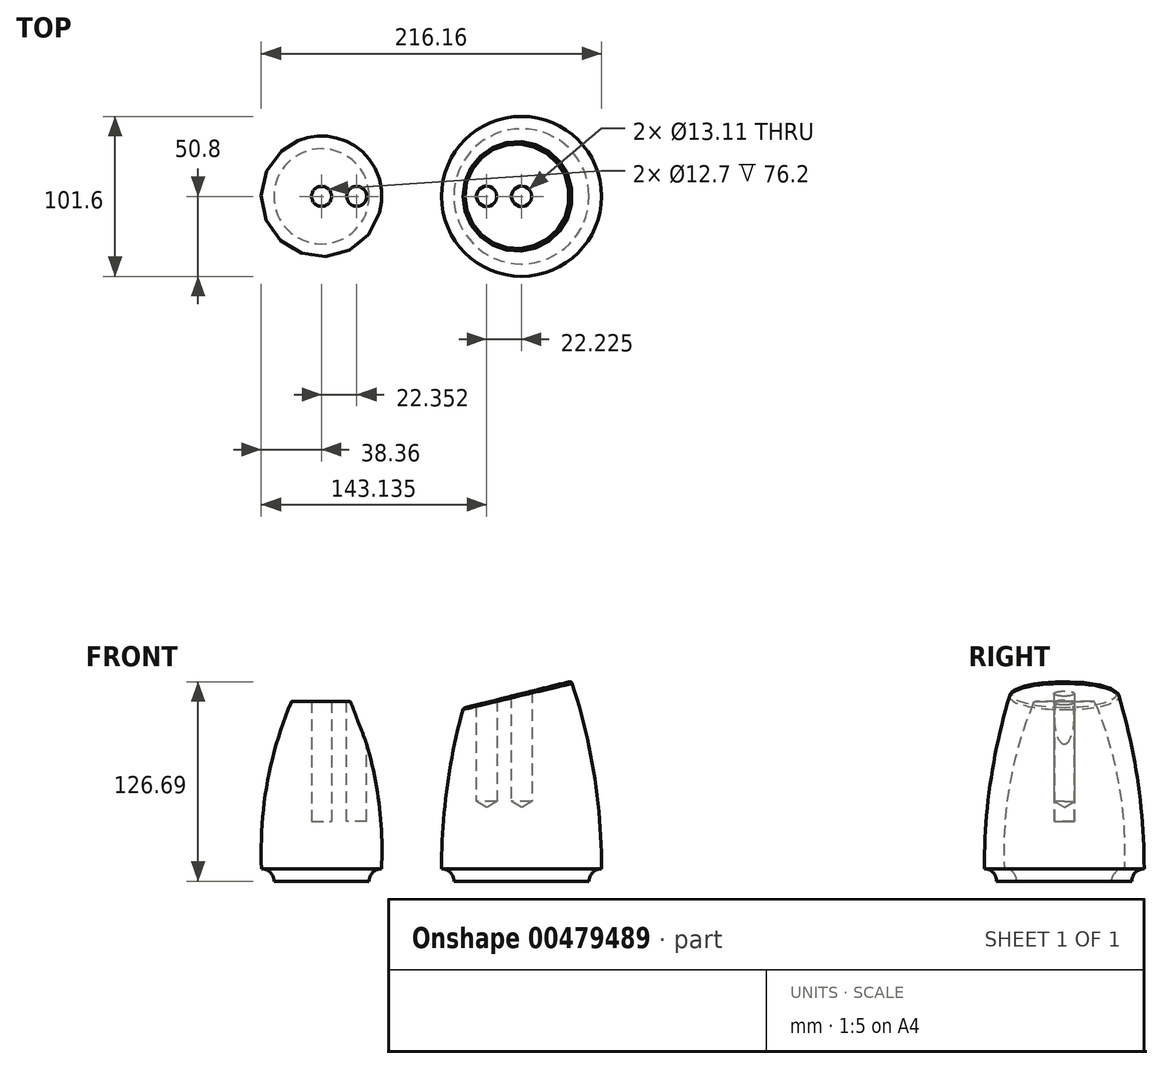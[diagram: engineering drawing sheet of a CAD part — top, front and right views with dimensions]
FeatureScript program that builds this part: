
annotation { "Feature Type Name" : "Feature", "Feature Type Description" : "" }
export const myFeature = defineFeature(function(context is Context, id is Id, definition is map)
    precondition{}
    {
        {
            var Q0;
            Q0=qCreatedBy(makeId("Front.planeOp"),FACE);
            var sketch = newSketch(context, id + "F0", { "sketchPlane" : qUnion([Q0])});
            skLineSegment(sketch, "E0", {"start": v(0, 0) * mm, "end": v(0, 152.4) * mm});
            skLineSegment(sketch, "E1", {"start": v(0, 0) * mm, "end": v(30.23, 0) * mm});
            skLineSegment(sketch, "E2", {"start": v(0, 114.3) * mm, "end": v(19.05, 114.3) * mm});
            skArc(sketch, "E3", {"start": v(38.1, 7.87) * mm, "mid": v(34.53, 62.15) * mm, "end": v(19.05, 114.3) * mm});
            skArc(sketch, "E4", {"start": v(38.1, 7.87) * mm, "mid": v(32.53, 5.57) * mm, "end": v(30.23, 0) * mm});
            skLineSegment(sketch, "E5.bottom", {"start": v(16, 114.3) * mm, "end": v(28.7, 114.3) * mm});
            skLineSegment(sketch, "E5.top", {"start": v(16, 38.1) * mm, "end": v(28.7, 38.1) * mm});
            skLineSegment(sketch, "E5.left", {"start": v(16, 114.3) * mm, "end": v(16, 38.1) * mm});
            skLineSegment(sketch, "E5.right", {"start": v(28.7, 114.3) * mm, "end": v(28.7, 38.1) * mm});
            skLineSegment(sketch, "E6", {"start": v(22.35, 38.1) * mm, "end": v(22.35, 114.3) * mm});
            skLineSegment(sketch, "E7", {"start": v(6.35, 114.3) * mm, "end": v(6.35, 38.1) * mm});
            skLineSegment(sketch, "E8", {"start": v(6.35, 38.1) * mm, "end": v(0, 38.1) * mm});
            skSolve(sketch);
        }
        {
            var Q0;
            {var subQ5=sQuery(id+"F0.wireOp",EDGE,"E1");Q0=makeQuery(id+"F0.imprint","IMPRINT",FACE,{"disambiguationData":[TD([[makeQuery(id+"F0.imprint","IMPRINT",EDGE,{"derivedFrom":subQ5}),1.0]])]});}
            var Q1;
            {var subQ5=sQuery(id+"F0.wireOp",EDGE,"E5.top");Q1=makeQuery(id+"F0.imprint","IMPRINT",FACE,{"disambiguationData":[TD([[makeQuery(id+"F0.imprint","IMPRINT",EDGE,{"derivedFrom":subQ5}),1.0]])]});}
            var Q2;
            {var subQ0=sQuery(id+"F0.wireOp",EDGE,"E5.left");Q2=makeQuery(id+"F0.imprint","IMPRINT",FACE,{"disambiguationData":[TD([[makeQuery(id+"F0.imprint","IMPRINT",EDGE,{"derivedFrom":subQ0}),1.0]])]});}
            var Q3;
            Q3=sQuery(id+"F0.wireOp",EDGE,"E0");
            revolve(context, id + "F1", {"entities" : qUnion([Q0, Q1, Q2]), "axis" : qUnion([Q3]), "revolveType" : RevolveType.FULL});
        }
        {
            var Q0;
            {var subQ4=sQuery(id+"F0.wireOp",EDGE,"E7");Q0=makeQuery(id+"F0.imprint","IMPRINT",FACE,{"disambiguationData":[TD([[makeQuery(id+"F0.imprint","IMPRINT",EDGE,{"derivedFrom":subQ4}),-1.0]])]});}
            var Q1;
            Q1=sQuery(id+"F0.wireOp",EDGE,"E0");
            revolve(context, id + "F2", {"operationType" : NewBodyOperationType.REMOVE, "entities" : qUnion([Q0]), "axis" : qUnion([Q1]), "revolveType" : RevolveType.FULL, "oppositeDirection" : true});
        }
        {
            var Q0;
            {var subQ0=sQuery(id+"F0.wireOp",EDGE,"E5.right");var subQ1=sQuery(id+"F0.wireOp",EDGE,"E3");var subQ2=makeQuery(id+"F0.imprint","INTERSECT",VERTEX,{"derivedFrom":[subQ1,subQ0]});Q0=makeQuery(id+"F0.imprint","IMPRINT",FACE,{"disambiguationData":[TD([[makeQuery(id+"F0.imprint","IMPRINT",EDGE,{"disambiguationData":[TD([[subQ2,-1.0]])],"derivedFrom":subQ1}),-1.0]])]});}
            var Q1;
            {var subQ0=sQuery(id+"F0.wireOp",EDGE,"E5.right");var subQ1=sQuery(id+"F0.wireOp",EDGE,"E3");var subQ2=makeQuery(id+"F0.imprint","INTERSECT",VERTEX,{"derivedFrom":[subQ1,subQ0]});Q1=makeQuery(id+"F0.imprint","IMPRINT",FACE,{"disambiguationData":[TD([[makeQuery(id+"F0.imprint","IMPRINT",EDGE,{"disambiguationData":[TD([[subQ2,-1.0]])],"derivedFrom":subQ1}),1.0]])]});}
            var Q2;
            Q2=sQuery(id+"F0.wireOp",EDGE,"E6");
            revolve(context, id + "F3", {"operationType" : NewBodyOperationType.REMOVE, "entities" : qUnion([Q0, Q1]), "axis" : qUnion([Q2]), "revolveType" : RevolveType.FULL, "oppositeDirection" : true});
        }
        {
            var Q0;
            {var subQ0=sQuery(id+"F0.wireOp",EDGE,"E5.bottom");var subQ2=sQuery(id+"F0.wireOp",EDGE,"E5.right");var subQ3=sQuery(id+"F0.wireOp",EDGE,"E3");var subQ5=makeQuery(id+"F3.boolean.opBoolean","COPY",FACE,{"derivedFrom":makeQuery(id+"F3.opRevolve","SWEPT_FACE",FACE,{"disambiguationData":[OSD([subQ2])]})});Q0=makeQuery(id+"F1Nw9IQKKF3mM8D_1.5.F3.boolean.opBoolean","SPLIT",EDGE,{"disambiguationData":[TD([subQ5])],"derivedFrom":makeQuery(id+"F1Nw9IQKKF3mM8D_1.4.F3.boolean.opBoolean","SPLIT",EDGE,{"disambiguationData":[TD([subQ5])],"derivedFrom":makeQuery(id+"F1Nw9IQKKF3mM8D_1.3.F3.boolean.opBoolean","SPLIT",EDGE,{"disambiguationData":[TD([subQ5])],"derivedFrom":makeQuery(id+"F1Nw9IQKKF3mM8D_1.2.F3.boolean.opBoolean","SPLIT",EDGE,{"disambiguationData":[TD([subQ5])],"derivedFrom":makeQuery(id+"F1Nw9IQKKF3mM8D_1.1.F3.boolean.opBoolean","SPLIT",EDGE,{"disambiguationData":[OD(0.0)],"derivedFrom":makeQuery(id+"F1.opRevolve","SWEPT_EDGE",EDGE,{"disambiguationData":[OSD([subQ3,subQ0])]})})})})})});}
            var Q1;
            {var subQ0=sQuery(id+"F0.wireOp",EDGE,"E5.bottom");var subQ2=sQuery(id+"F0.wireOp",EDGE,"E5.right");var subQ3=sQuery(id+"F0.wireOp",EDGE,"E3");var subQ5=makeQuery(id+"F1Nw9IQKKF3mM8D_1.4.F3.opRevolve","SWEPT_FACE",FACE,{"disambiguationData":[OSD([subQ2])]});var subQ6=makeQuery(id+"F3.boolean.opBoolean","COPY",FACE,{"derivedFrom":makeQuery(id+"F3.opRevolve","SWEPT_FACE",FACE,{"disambiguationData":[OSD([subQ2])]})});Q1=makeQuery(id+"F1Nw9IQKKF3mM8D_1.5.F3.boolean.opBoolean","SPLIT",EDGE,{"disambiguationData":[TD([makeQuery(id+"F1Nw9IQKKF3mM8D_1.4.F3.boolean.opBoolean","COPY",FACE,{"derivedFrom":subQ5})])],"derivedFrom":makeQuery(id+"F1Nw9IQKKF3mM8D_1.4.F3.boolean.opBoolean","SPLIT",EDGE,{"disambiguationData":[TD([subQ6])],"derivedFrom":makeQuery(id+"F1Nw9IQKKF3mM8D_1.3.F3.boolean.opBoolean","SPLIT",EDGE,{"disambiguationData":[TD([subQ6])],"derivedFrom":makeQuery(id+"F1Nw9IQKKF3mM8D_1.2.F3.boolean.opBoolean","SPLIT",EDGE,{"disambiguationData":[TD([subQ6])],"derivedFrom":makeQuery(id+"F1Nw9IQKKF3mM8D_1.1.F3.boolean.opBoolean","SPLIT",EDGE,{"disambiguationData":[OD(0.0)],"derivedFrom":makeQuery(id+"F1.opRevolve","SWEPT_EDGE",EDGE,{"disambiguationData":[OSD([subQ3,subQ0])]})})})})})});}
            var Q2;
            {var subQ0=sQuery(id+"F0.wireOp",EDGE,"E5.bottom");var subQ2=sQuery(id+"F0.wireOp",EDGE,"E5.right");var subQ3=makeQuery(id+"F1Nw9IQKKF3mM8D_1.3.F3.opRevolve","SWEPT_FACE",FACE,{"disambiguationData":[OSD([subQ2])]});var subQ4=sQuery(id+"F0.wireOp",EDGE,"E3");var subQ6=makeQuery(id+"F3.boolean.opBoolean","COPY",FACE,{"derivedFrom":makeQuery(id+"F3.opRevolve","SWEPT_FACE",FACE,{"disambiguationData":[OSD([subQ2])]})});Q2=makeQuery(id+"F1Nw9IQKKF3mM8D_1.4.F3.boolean.opBoolean","SPLIT",EDGE,{"disambiguationData":[TD([makeQuery(id+"F1Nw9IQKKF3mM8D_1.3.F3.boolean.opBoolean","COPY",FACE,{"derivedFrom":subQ3})])],"derivedFrom":makeQuery(id+"F1Nw9IQKKF3mM8D_1.3.F3.boolean.opBoolean","SPLIT",EDGE,{"disambiguationData":[TD([subQ6])],"derivedFrom":makeQuery(id+"F1Nw9IQKKF3mM8D_1.2.F3.boolean.opBoolean","SPLIT",EDGE,{"disambiguationData":[TD([subQ6])],"derivedFrom":makeQuery(id+"F1Nw9IQKKF3mM8D_1.1.F3.boolean.opBoolean","SPLIT",EDGE,{"disambiguationData":[OD(0.0)],"derivedFrom":makeQuery(id+"F1.opRevolve","SWEPT_EDGE",EDGE,{"disambiguationData":[OSD([subQ4,subQ0])]})})})})});}
            var Q3;
            {var subQ0=sQuery(id+"F0.wireOp",EDGE,"E5.bottom");var subQ2=sQuery(id+"F0.wireOp",EDGE,"E3");var subQ4=sQuery(id+"F0.wireOp",EDGE,"E5.right");var subQ5=makeQuery(id+"F1Nw9IQKKF3mM8D_1.2.F3.opRevolve","SWEPT_FACE",FACE,{"disambiguationData":[OSD([subQ4])]});Q3=makeQuery(id+"F1Nw9IQKKF3mM8D_1.3.F3.boolean.opBoolean","SPLIT",EDGE,{"disambiguationData":[TD([makeQuery(id+"F1Nw9IQKKF3mM8D_1.2.F3.boolean.opBoolean","COPY",FACE,{"derivedFrom":subQ5})])],"derivedFrom":makeQuery(id+"F1Nw9IQKKF3mM8D_1.2.F3.boolean.opBoolean","SPLIT",EDGE,{"disambiguationData":[TD([makeQuery(id+"F3.boolean.opBoolean","COPY",FACE,{"derivedFrom":makeQuery(id+"F3.opRevolve","SWEPT_FACE",FACE,{"disambiguationData":[OSD([subQ4])]})})])],"derivedFrom":makeQuery(id+"F1Nw9IQKKF3mM8D_1.1.F3.boolean.opBoolean","SPLIT",EDGE,{"disambiguationData":[OD(0.0)],"derivedFrom":makeQuery(id+"F1.opRevolve","SWEPT_EDGE",EDGE,{"disambiguationData":[OSD([subQ2,subQ0])]})})})});}
            var Q4;
            {var subQ0=sQuery(id+"F0.wireOp",EDGE,"E5.bottom");var subQ1=sQuery(id+"F0.wireOp",EDGE,"E3");var subQ2=sQuery(id+"F0.wireOp",EDGE,"E5.right");Q4=makeQuery(id+"F1Nw9IQKKF3mM8D_1.2.F3.boolean.opBoolean","SPLIT",EDGE,{"disambiguationData":[TD([makeQuery(id+"F1Nw9IQKKF3mM8D_1.1.F3.boolean.opBoolean","COPY",FACE,{"derivedFrom":makeQuery(id+"F1Nw9IQKKF3mM8D_1.1.F3.opRevolve","SWEPT_FACE",FACE,{"disambiguationData":[OSD([subQ2])]})})])],"derivedFrom":makeQuery(id+"F1Nw9IQKKF3mM8D_1.1.F3.boolean.opBoolean","SPLIT",EDGE,{"disambiguationData":[OD(0.0)],"derivedFrom":makeQuery(id+"F1.opRevolve","SWEPT_EDGE",EDGE,{"disambiguationData":[OSD([subQ1,subQ0])]})})});}
            var Q5;
            Q5=makeQuery(id+"F1Nw9IQKKF3mM8D_1.1.F3.boolean.opBoolean","SPLIT",EDGE,{"disambiguationData":[OD(1.0)],"derivedFrom":makeQuery(id+"F1.opRevolve","SWEPT_EDGE",EDGE,{"disambiguationData":[OSD([sQuery(id+"F0.wireOp",EDGE,"E3"),sQuery(id+"F0.wireOp",EDGE,"E5.bottom")])]})});
            fillet(context, id + "F4", {"entities" : qUnion([Q0, Q1, Q2, Q3, Q4, Q5]), "radius" : 1.6 * mm, "tangentPropagation" : true, "allowEdgeOverflow" : false});
        }
        {
            var Q0;
            Q0=qCreatedBy(makeId("Front.planeOp"),FACE);
            var sketch = newSketch(context, id + "F5", { "sketchPlane" : qUnion([Q0])});
            skLineSegment(sketch, "E9.bottom", {"start": v(127, 0) * mm, "end": v(76.2, 0) * mm});
            skLineSegment(sketch, "E9.top", {"start": v(127, 127) * mm, "end": v(76.2, 127) * mm});
            skLineSegment(sketch, "E9.left", {"start": v(127, 0) * mm, "end": v(127, 127) * mm});
            skLineSegment(sketch, "E9.right", {"start": v(76.2, 0) * mm, "end": v(76.2, 127) * mm});
            skArc(sketch, "E10", {"start": v(95.25, 127) * mm, "mid": v(81, 68.2) * mm, "end": v(76.2, 7.87) * mm});
            skArc(sketch, "E11", {"start": v(84.07, 0) * mm, "mid": v(81.77, 5.57) * mm, "end": v(76.2, 7.87) * mm});
            skLineSegment(sketch, "E12", {"start": v(158.75, 127) * mm, "end": v(76.2, 106.42) * mm});
            skLineSegment(sketch, "E13", {"start": v(127, 127) * mm, "end": v(158.75, 127) * mm});
            skSolve(sketch);
        }
        {
            var Q0;
            {var subQ0=sQuery(id+"F5.wireOp",EDGE,"E11");Q0=makeQuery(id+"F5.imprint","IMPRINT",FACE,{"disambiguationData":[TD([[makeQuery(id+"F5.imprint","IMPRINT",EDGE,{"derivedFrom":subQ0}),-1.0]])]});}
            var Q1;
            {var subQ1=sQuery(id+"F5.wireOp",EDGE,"E9.top");var subQ3=sQuery(id+"F5.wireOp",EDGE,"E10");var subQ4=makeQuery(id+"F5.imprint","INTERSECT",VERTEX,{"derivedFrom":[subQ1,subQ3]});Q1=makeQuery(id+"F5.imprint","IMPRINT",FACE,{"disambiguationData":[TD([[makeQuery(id+"F5.imprint","IMPRINT",EDGE,{"disambiguationData":[TD([[subQ4,-1.0]])],"derivedFrom":subQ3}),1.0]])]});}
            var Q2;
            Q2=sQuery(id+"F5.wireOp",EDGE,"E9.left");
            revolve(context, id + "F6", {"entities" : qUnion([Q0, Q1]), "axis" : qUnion([Q2]), "revolveType" : RevolveType.FULL});
        }
        {
            var Q0;
            Q0=makeQuery(id+"F6.opRevolve","SWEPT_FACE",FACE,{"disambiguationData":[OSD([sQuery(id+"F5.wireOp",EDGE,"E9.top")])]});
            var sketch = newSketch(context, id + "F7", { "sketchPlane" : qUnion([Q0])});
            skPoint(sketch, "E14", {"position": v(127, 0) * mm});
            skPoint(sketch, "E15", {"position": v(104.77, 0) * mm});
            skSolve(sketch);
        }
        {
            var Q0;
            Q0=sQuery(id+"F7.wireOp",VERTEX,"E14");
            var Q1;
            Q1=sQuery(id+"F7.wireOp",VERTEX,"E15");
            var Q2;
            Q2=makeQuery(id+"F6.opRevolve","SWEPT_BODY",BODY,{"disambiguationData":[OSD([sQuery(id+"F5.wireOp",EDGE,"E9.bottom"),sQuery(id+"F5.wireOp",EDGE,"E9.top"),sQuery(id+"F5.wireOp",EDGE,"E9.left"),sQuery(id+"F5.wireOp",EDGE,"E10"),sQuery(id+"F5.wireOp",EDGE,"E11")])]});
            hole(context, id + "F8", {"style" : HoleStyle.SIMPLE, "endStyle" : HoleEndStyle.BLIND, "standardTappedOrClearance" : lookupTablePath({ "standard" : "ANSI", "fit" : "Close", "size" : "1/2", "type" : "Clearance" }), "standardBlindInLast" : lookupTablePath({ "fit" : "Close", "standard" : "ANSI", "size" : "1/2", "type" : "Clearance" }), "holeDiameter" : 13.1 * mm, "holeDepth" : 76.2 * mm, "isTappedThrough" : true, "tappedDepth" : 12.7 * mm, "tapClearance" : 3, "startFromSketch" : true, "locations" : qUnion([Q0, Q1]), "scope" : qUnion([Q2])});
        }
        {
            var Q0;
            {var subQ0=sQuery(id+"F5.wireOp",EDGE,"E9.right");var subQ1=sQuery(id+"F5.wireOp",EDGE,"E9.top");var subQ2=makeQuery(id+"F5.imprint","INTERSECT",VERTEX,{"derivedFrom":[subQ1,subQ0]});Q0=makeQuery(id+"F5.imprint","IMPRINT",FACE,{"disambiguationData":[TD([[makeQuery(id+"F5.imprint","IMPRINT",EDGE,{"disambiguationData":[TD([[subQ2,1.0]])],"derivedFrom":subQ1}),1.0]])]});}
            var Q1;
            {var subQ1=sQuery(id+"F5.wireOp",EDGE,"E9.top");var subQ3=sQuery(id+"F5.wireOp",EDGE,"E10");var subQ4=makeQuery(id+"F5.imprint","INTERSECT",VERTEX,{"derivedFrom":[subQ1,subQ3]});Q1=makeQuery(id+"F5.imprint","IMPRINT",FACE,{"disambiguationData":[TD([[makeQuery(id+"F5.imprint","IMPRINT",EDGE,{"disambiguationData":[TD([[subQ4,-1.0]])],"derivedFrom":subQ3}),1.0]])]});}
            var Q2;
            {var subQ0=sQuery(id+"F5.wireOp",EDGE,"E13");Q2=makeQuery(id+"F5.imprint","IMPRINT",FACE,{"disambiguationData":[TD([[makeQuery(id+"F5.imprint","IMPRINT",EDGE,{"derivedFrom":subQ0}),-1.0]])]});}
            extrude(context, id + "F9", {"entities" : qUnion([Q0, Q1, Q2]), "operationType" : NewBodyOperationType.REMOVE, "endBound" : BoundingType.THROUGH_ALL, "oppositeDirection" : true, "depth" : 25.4 * mm, "hasSecondDirection" : true, "secondDirectionBound" : BoundingType.THROUGH_ALL, "secondDirectionOppositeDirection" : false, "secondDirectionDepth" : 25.4 * mm});
        }
        {
            var Q0;
            Q0=makeQuery(id+"F9.boolean.opBoolean","INTERSECT",EDGE,{"derivedFrom":[makeQuery(id+"F6.opRevolve","SWEPT_FACE",FACE,{"disambiguationData":[OSD([sQuery(id+"F5.wireOp",EDGE,"E10")])]}),makeQuery(id+"F9.opExtrude","SWEPT_FACE",FACE,{"disambiguationData":[OSD([sQuery(id+"F5.wireOp",EDGE,"E12")])]})]});
            fillet(context, id + "F10", {"entities" : qUnion([Q0]), "radius" : 1.6 * mm, "tangentPropagation" : true, "allowEdgeOverflow" : false});
        }
    });
